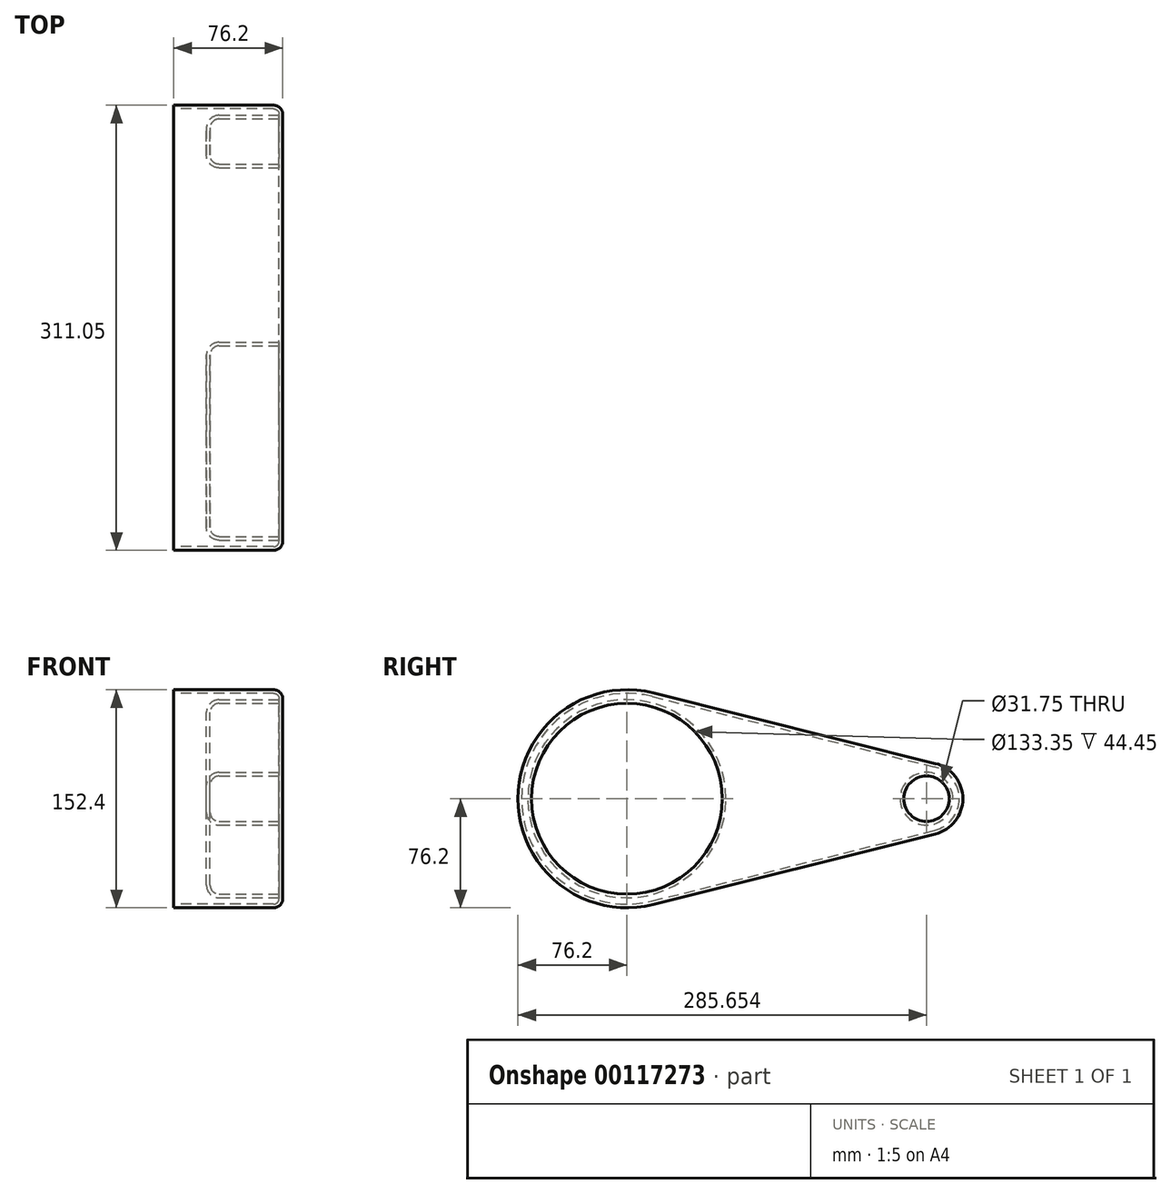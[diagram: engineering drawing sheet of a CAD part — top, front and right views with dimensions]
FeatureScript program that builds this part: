
annotation { "Feature Type Name" : "Feature", "Feature Type Description" : "" }
export const myFeature = defineFeature(function(context is Context, id is Id, definition is map)
    precondition{}
    {
        {
            var Q0;
            Q0=qCreatedBy(makeId("Right.planeOp"),FACE);
            var sketch = newSketch(context, id + "F0", { "sketchPlane" : qUnion([Q0])});
            skCircle(sketch, "E0", {"center": v(0, 0) * mm, "radius": 76.2 * mm});
            skCircle(sketch, "E1", {"center": v(209.45, 0) * mm, "radius": 25.4 * mm});
            skLineSegment(sketch, "E2", {"start": v(18.48, 73.92) * mm, "end": v(215.61, 24.64) * mm});
            skLineSegment(sketch, "E3", {"start": v(18.48, -73.92) * mm, "end": v(215.61, -24.64) * mm});
            skSolve(sketch);
        }
        {
            var Q0;
            {var subQ0=sQuery(id+"F0.wireOp",EDGE,"E0");var subQ1=makeQuery(id+"F0.imprint","INTERSECT",VERTEX,{"derivedFrom":[subQ0,sQuery(id+"F0.wireOp",EDGE,"E2")]});Q0=makeQuery(id+"F0.imprint","IMPRINT",FACE,{"disambiguationData":[TD([[makeQuery(id+"F0.imprint","IMPRINT",EDGE,{"disambiguationData":[TD([[subQ1,-1.0]])],"derivedFrom":subQ0}),1.0]])]});}
            var Q1;
            {var subQ0=sQuery(id+"F0.wireOp",EDGE,"E2");Q1=makeQuery(id+"F0.imprint","IMPRINT",FACE,{"disambiguationData":[TD([[makeQuery(id+"F0.imprint","IMPRINT",EDGE,{"derivedFrom":subQ0}),-1.0]])]});}
            var Q2;
            {var subQ0=sQuery(id+"F0.wireOp",EDGE,"E1");var subQ1=makeQuery(id+"F0.imprint","INTERSECT",VERTEX,{"derivedFrom":[subQ0,sQuery(id+"F0.wireOp",EDGE,"E2")]});Q2=makeQuery(id+"F0.imprint","IMPRINT",FACE,{"disambiguationData":[TD([[makeQuery(id+"F0.imprint","IMPRINT",EDGE,{"disambiguationData":[TD([[subQ1,-1.0]])],"derivedFrom":subQ0}),1.0]])]});}
            var Q3;
            Q3 = qSketchRegion(id + "F2", true);
            extrude(context, id + "F1", {"entities" : qUnion([Q0, Q1, Q2, Q3]), "depth" : 76.2 * mm});
        }
        {
            var Q0;
            Q0=makeQuery(id+"F1.opExtrude","CAP_FACE",FACE,{"disambiguationData":[OSD([sQuery(id+"F0.wireOp",EDGE,"E0"),sQuery(id+"F0.wireOp",EDGE,"E1"),sQuery(id+"F0.wireOp",EDGE,"E2"),sQuery(id+"F0.wireOp",EDGE,"E3")])],"isStart":false});
            var sketch = newSketch(context, id + "F2", { "sketchPlane" : qUnion([Q0])});
            skCircle(sketch, "E4", {"center": v(0, 0) * mm, "radius": 66.68 * mm});
            skCircle(sketch, "E5", {"center": v(209.45, 0) * mm, "radius": 15.88 * mm});
            skSolve(sketch);
        }
        {
            var Q0;
            Q0=makeQuery(id+"F2.imprint","IMPRINT",FACE,{"disambiguationData":[TD([[makeQuery(id+"F2.imprint","IMPRINT",EDGE,{"derivedFrom":sQuery(id+"F2.wireOp",EDGE,"E4")}),1.0]])]});
            var Q1;
            Q1=makeQuery(id+"F2.imprint","IMPRINT",FACE,{"disambiguationData":[TD([[makeQuery(id+"F2.imprint","IMPRINT",EDGE,{"derivedFrom":sQuery(id+"F2.wireOp",EDGE,"E5")}),1.0]])]});
            extrude(context, id + "F3", {"entities" : qUnion([Q0, Q1]), "operationType" : NewBodyOperationType.REMOVE, "oppositeDirection" : true, "depth" : 50.8 * mm});
        }
        {
            var Q0;
            Q0=makeQuery(id+"F3.boolean.opBoolean","COPY",EDGE,{"derivedFrom":makeQuery(id+"F3.opExtrude","CAP_EDGE",EDGE,{"disambiguationData":[OSD([sQuery(id+"F2.wireOp",EDGE,"E4")])],"isStart":false})});
            var Q1;
            Q1=makeQuery(id+"F3.boolean.opBoolean","COPY",EDGE,{"derivedFrom":makeQuery(id+"F3.opExtrude","CAP_EDGE",EDGE,{"disambiguationData":[OSD([sQuery(id+"F2.wireOp",EDGE,"E5")])],"isStart":false})});
            var Q2;
            Q2=makeQuery(id+"F3.boolean.opBoolean","COPY",EDGE,{"derivedFrom":makeQuery(id+"F3.opExtrude","CAP_EDGE",EDGE,{"disambiguationData":[OSD([sQuery(id+"F2.wireOp",EDGE,"E4")])],"isStart":true})});
            var Q3;
            Q3=makeQuery(id+"F3.boolean.opBoolean","COPY",EDGE,{"derivedFrom":makeQuery(id+"F3.opExtrude","CAP_EDGE",EDGE,{"disambiguationData":[OSD([sQuery(id+"F2.wireOp",EDGE,"E5")])],"isStart":true})});
            var Q4;
            Q4=makeQuery(id+"F1.opExtrude","CAP_EDGE",EDGE,{"disambiguationData":[OSD([sQuery(id+"F0.wireOp",EDGE,"E3")])],"isStart":false});
            fillet(context, id + "F4", {"entities" : qUnion([Q0, Q1, Q2, Q3, Q4]), "radius" : 6.35 * mm, "tangentPropagation" : true, "allowEdgeOverflow" : false});
        }
        {
            var Q0;
            Q0=makeQuery(id+"F1.opExtrude","CAP_FACE",FACE,{"disambiguationData":[OSD([sQuery(id+"F0.wireOp",EDGE,"E0"),sQuery(id+"F0.wireOp",EDGE,"E1"),sQuery(id+"F0.wireOp",EDGE,"E2"),sQuery(id+"F0.wireOp",EDGE,"E3")])],"isStart":true});
            shell(context, id + "F5", {"entities" : qUnion([Q0]), "thickness" : 2.54 * mm});
        }
    });
